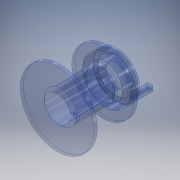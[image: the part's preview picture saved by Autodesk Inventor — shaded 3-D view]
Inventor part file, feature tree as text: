
AUTODESK INVENTOR PART (.ipt)
format: ipt  version: 2018 (Build 220112000, 112)  size: 435,712 bytes
history: native  units: mm
features: sketch x15, extrude x14, projected_geometry x2, pattern_circular x1, plane x1
ambient origin geometry x8: Origin, YZ Plane, XZ Plane, XY Plane, X Axis, Y Axis, Z Axis, Center Point
bodies: 实体1 (feature_tree)
feature tree (33):
  extrude  "拉伸1"  Depth=3.0mm TaperAngle=0.0deg
  extrude  "拉伸2"  Depth=25.0mm
  extrude  "拉伸3"  Depth=60.0mm
  extrude  "拉伸4"  Depth=3.0mm TaperAngle=0.0deg
  extrude  "拉伸5"  Depth=5.0mm TaperAngle=0.0deg
  extrude  "拉伸6"  Depth=45.0mm
  extrude  "拉伸7"  Depth=10.0mm
  extrude  "拉伸8"  Depth=3.0mm TaperAngle=0.0deg
  pattern_circular  "环形阵列1"  Count=2 Angle=360.0deg
  extrude  "拉伸9"  Depth=5.0mm
  extrude  "拉伸10"  Depth=5.0mm
  extrude  "拉伸11"  Depth=10.0mm
  extrude  "拉伸12"  Depth=13.5mm
  extrude  "拉伸13"  Depth=1.5mm
  plane  "工作平面2"
  sketch  "草图14"  dims[d40=13.0mm d41=13.5mm]
  extrude  "拉伸14"  Depth=17.5mm TaperAngle=0.0deg
  sketch  "草图1"  dims[d0=71.0mm d1=3.0mm d2=0.0mm]
  sketch  "草图2"  dims[d3=31.0mm d4=25.0mm]
  sketch  "草图3"  dims[d5=41.0mm d6=0.0mm d7=60.0mm]
  sketch  "草图4"  dims[d8=3.0mm d9=0.0mm d10=3.0mm d11=0.0mm]
  sketch  "草图5"  dims[d12=7.0mm d13=5.0mm d14=0.0mm]
  sketch  "草图6"  dims[d15=20.0mm d16=45.0mm]
  sketch  "草图7"  dims[d17=10.0mm d18=0.0mm d19=45.0mm]
  sketch  "草图8"  dims[d20=7.0mm d21=3.0mm d22=0.0mm]
  sketch  "草图9"  dims[d23=5.0mm]
  sketch  "草图10"  dims[d24=3.0mm d25=0.0mm d26=20.0mm d27=360.0deg]
  sketch  "草图11"  dims[d30=16.0mm d31=0.0mm d32=5.0mm]
  projected_geometry  "投影回路1"
  sketch  "草图12"  dims[d33=5.0mm d34=24.0mm]
  sketch  "草图13"  dims[d36=10.0mm d38=22.0mm]
  projected_geometry  "投影回路2"
  sketch  "草图15"  dims[d42=4.0mm d43=0.0mm d44=1.5mm d45=17.5mm d46=0.0mm d47=2.0mm d48=2.0mm d49=0.0mm d50=3.0mm d51=0.0mm d52=9.0mm d53=9.0mm d56=1.0mm d57=-1.0mm d58=1.0mm d59=10.0mm d60=0.0mm]
